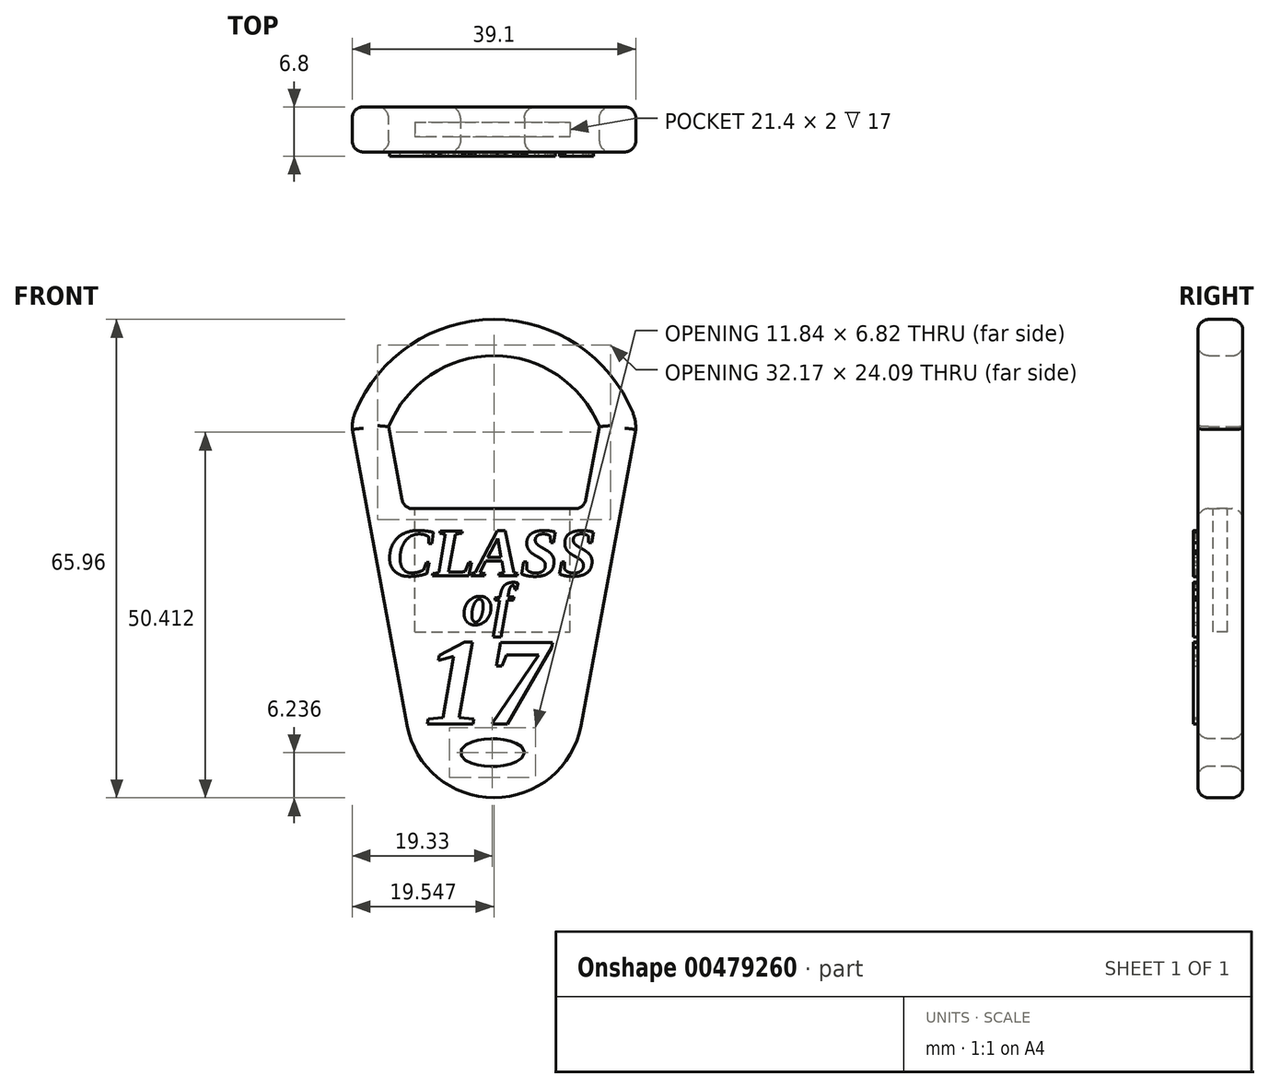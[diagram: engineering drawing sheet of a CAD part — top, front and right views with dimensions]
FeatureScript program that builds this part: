
annotation { "Feature Type Name" : "Feature", "Feature Type Description" : "" }
export const myFeature = defineFeature(function(context is Context, id is Id, definition is map)
    precondition{}
    {
        {
            var Q0;
            Q0=qCreatedBy(makeId("Front.planeOp"),FACE);
            var sketch = newSketch(context, id + "F0", { "sketchPlane" : qUnion([Q0])});
            skLineSegment(sketch, "E0", {"start": v(0.22, 53.5) * mm, "end": v(0.22, -27.22) * mm, "construction": true});
            skLineSegment(sketch, "E1", {"start": v(19.76, 12.33) * mm, "end": v(12.22, -28.48) * mm});
            skLineSegment(sketch, "E2.MirrorCS", {"start": v(-19.33, 12.33) * mm, "end": v(-11.78, -28.48) * mm});
            skLineSegment(sketch, "E3.0", {"start": v(-14.31, 12.71) * mm, "end": v(-12.22, 1.4) * mm});
            skLineSegment(sketch, "E3.3", {"start": v(14.75, 12.71) * mm, "end": v(12.66, 1.4) * mm});
            skLineSegment(sketch, "E4", {"start": v(-12.22, 1.4) * mm, "end": v(12.66, 1.4) * mm});
            skPoint(sketch, "E5", {"position": v(0.22, 20.6) * mm});
            skPoint(sketch, "E6", {"position": v(-14.31, 12.71) * mm});
            skPoint(sketch, "E7.MirrorP", {"position": v(14.75, 12.71) * mm});
            skArc(sketch, "E8", {"start": v(14.75, 12.71) * mm, "mid": v(0.22, 22.5) * mm, "end": v(-14.31, 12.71) * mm});
            skArc(sketch, "E9.0", {"start": v(19.62, 13.97) * mm, "mid": v(0.56, 27.5) * mm, "end": v(-18.94, 14.6) * mm});
            skArc(sketch, "E10", {"start": v(-18.94, 14.6) * mm, "mid": v(-19.26, 13.5) * mm, "end": v(-19.33, 12.33) * mm});
            skArc(sketch, "E11.MirrorCS", {"start": v(19.38, 14.6) * mm, "mid": v(19.7, 13.5) * mm, "end": v(19.76, 12.33) * mm});
            skPoint(sketch, "E12.orphan", {"position": v(-21.9, 26.19) * mm});
            skPoint(sketch, "E13.orphan", {"position": v(22.32, 26.19) * mm});
            skPoint(sketch, "E14.MirrorCS.start.orphan", {"position": v(0.22, 25.6) * mm});
            skArc(sketch, "E15", {"start": v(-11.78, -28.48) * mm, "mid": v(0.22, -38.46) * mm, "end": v(12.22, -28.48) * mm});
            skPoint(sketch, "E16.MirrorCS.end.orphan", {"position": v(0.22, -28.48) * mm});
            skPoint(sketch, "E16.MirrorCS.start.orphan", {"position": v(-11.78, -28.48) * mm});
            skLineSegment(sketch, "E17", {"start": v(-11.78, -28.48) * mm, "end": v(12.22, -28.48) * mm, "construction": true});
            skSolve(sketch);
        }
        {
            var Q0;
            Q0=qSketchRegion(id+"F0",true);
            extrude(context, id + "F1", {"entities" : qUnion([Q0]), "depth" : 6.2 * mm});
        }
        {
            var Q0;
            Q0=makeQuery(id+"F1.opExtrude","CAP_FACE",FACE,{"disambiguationData":[OSD([sQuery(id+"F0.wireOp",EDGE,"E1"),sQuery(id+"F0.wireOp",EDGE,"E2.MirrorCS"),sQuery(id+"F0.wireOp",EDGE,"E3.0"),sQuery(id+"F0.wireOp",EDGE,"E3.3"),sQuery(id+"F0.wireOp",EDGE,"E4"),sQuery(id+"F0.wireOp",EDGE,"E8"),sQuery(id+"F0.wireOp",EDGE,"E9.0"),sQuery(id+"F0.wireOp",EDGE,"E10"),sQuery(id+"F0.wireOp",EDGE,"E11.MirrorCS"),sQuery(id+"F0.wireOp",EDGE,"E15")])],"isStart":false});
            var sketch = newSketch(context, id + "F2", { "sketchPlane" : qUnion([Q0])});
            skEllipse(sketch, "E18", {"center": v(0, -32.22) * mm, "majorRadius": 4.42 * mm, "minorRadius": 1.9 * mm, "majorAxis": v(1, 0)});
            skSolve(sketch);
        }
        {
            var Q0;
            Q0=makeQuery(id+"F2.imprint","IMPRINT",FACE,{"disambiguationData":[TD([[makeQuery(id+"F2.imprint","IMPRINT",EDGE,{"derivedFrom":sQuery(id+"F2.wireOp",EDGE,"E18")}),1.0]])]});
            extrude(context, id + "F3", {"entities" : qUnion([Q0]), "operationType" : NewBodyOperationType.REMOVE, "oppositeDirection" : true, "depth" : 6.5 * mm});
        }
        {
            var Q0;
            Q0=makeQuery(id+"F1.opExtrude","SWEPT_FACE",FACE,{"disambiguationData":[OSD([sQuery(id+"F0.wireOp",EDGE,"E4")])]});
            var sketch = newSketch(context, id + "F4", { "sketchPlane" : qUnion([Q0])});
            skLineSegment(sketch, "E19", {"start": v(0, -2.1) * mm, "end": v(10.7, -2.1) * mm});
            skLineSegment(sketch, "E20.0", {"start": v(0, -4.1) * mm, "end": v(10.7, -4.1) * mm});
            skLineSegment(sketch, "E21", {"start": v(10.7, -2.1) * mm, "end": v(10.7, -4.1) * mm});
            skLineSegment(sketch, "E22", {"start": v(0, -2.1) * mm, "end": v(0, -4.1) * mm, "construction": true});
            skLineSegment(sketch, "E23.MirrorCS", {"start": v(0, -2.1) * mm, "end": v(-10.7, -2.1) * mm});
            skLineSegment(sketch, "E24.MirrorCS", {"start": v(-10.7, -2.1) * mm, "end": v(-10.7, -4.1) * mm});
            skLineSegment(sketch, "E25.MirrorCS", {"start": v(0, -4.1) * mm, "end": v(-10.7, -4.1) * mm});
            skSolve(sketch);
        }
        {
            var Q0;
            Q0=makeQuery(id+"F4.imprint","IMPRINT",FACE,{"disambiguationData":[TD([[makeQuery(id+"F4.imprint","IMPRINT",EDGE,{"derivedFrom":sQuery(id+"F4.wireOp",EDGE,"E19")}),-1.0]])]});
            extrude(context, id + "F5", {"entities" : qUnion([Q0]), "operationType" : NewBodyOperationType.REMOVE, "oppositeDirection" : true, "depth" : 17 * mm});
        }
        {
            var Q0;
            Q0=makeQuery(id+"F1.opExtrude","SWEPT_EDGE",EDGE,{"disambiguationData":[OSD([sQuery(id+"F0.wireOp",EDGE,"E3.0"),sQuery(id+"F0.wireOp",EDGE,"E4")])]});
            var Q1;
            Q1=makeQuery(id+"F1.opExtrude","SWEPT_EDGE",EDGE,{"disambiguationData":[OSD([sQuery(id+"F0.wireOp",EDGE,"E3.3"),sQuery(id+"F0.wireOp",EDGE,"E4")])]});
            var Q2;
            Q2=makeQuery(id+"F1.opExtrude","CAP_FACE",FACE,{"disambiguationData":[OSD([sQuery(id+"F0.wireOp",EDGE,"E1"),sQuery(id+"F0.wireOp",EDGE,"E2.MirrorCS"),sQuery(id+"F0.wireOp",EDGE,"E3.0"),sQuery(id+"F0.wireOp",EDGE,"E3.3"),sQuery(id+"F0.wireOp",EDGE,"E4"),sQuery(id+"F0.wireOp",EDGE,"E8"),sQuery(id+"F0.wireOp",EDGE,"E9.0"),sQuery(id+"F0.wireOp",EDGE,"E10"),sQuery(id+"F0.wireOp",EDGE,"E11.MirrorCS"),sQuery(id+"F0.wireOp",EDGE,"E15")])],"isStart":false});
            var Q3;
            Q3=makeQuery(id+"F1.opExtrude","CAP_FACE",FACE,{"disambiguationData":[OSD([sQuery(id+"F0.wireOp",EDGE,"E1"),sQuery(id+"F0.wireOp",EDGE,"E2.MirrorCS"),sQuery(id+"F0.wireOp",EDGE,"E3.0"),sQuery(id+"F0.wireOp",EDGE,"E3.3"),sQuery(id+"F0.wireOp",EDGE,"E4"),sQuery(id+"F0.wireOp",EDGE,"E8"),sQuery(id+"F0.wireOp",EDGE,"E9.0"),sQuery(id+"F0.wireOp",EDGE,"E10"),sQuery(id+"F0.wireOp",EDGE,"E11.MirrorCS"),sQuery(id+"F0.wireOp",EDGE,"E15")])],"isStart":true});
            fillet(context, id + "F6", {"entities" : qUnion([Q0, Q1, Q2, Q3]), "radius" : 1.5 * mm, "tangentPropagation" : true, "allowEdgeOverflow" : false});
        }
        {
            var Q0;
            Q0=makeQuery(id+"F1.opExtrude","CAP_FACE",FACE,{"disambiguationData":[OSD([sQuery(id+"F0.wireOp",EDGE,"E1"),sQuery(id+"F0.wireOp",EDGE,"E2.MirrorCS"),sQuery(id+"F0.wireOp",EDGE,"E3.0"),sQuery(id+"F0.wireOp",EDGE,"E3.3"),sQuery(id+"F0.wireOp",EDGE,"E4"),sQuery(id+"F0.wireOp",EDGE,"E8"),sQuery(id+"F0.wireOp",EDGE,"E9.0"),sQuery(id+"F0.wireOp",EDGE,"E10"),sQuery(id+"F0.wireOp",EDGE,"E11.MirrorCS"),sQuery(id+"F0.wireOp",EDGE,"E15")])],"isStart":false});
            var sketch = newSketch(context, id + "F7", { "sketchPlane" : qUnion([Q0])});
            skText(sketch, "E26", { "text": "CLASS", "fontName": "Tinos-BoldItalic.ttf"});
            skText(sketch, "E27", { "text": "of", "fontName": "Tinos-BoldItalic.ttf"});
            skText(sketch, "E28", { "text": "17", "fontName": "Tinos-BoldItalic.ttf"});
            const initialGuessF7  = {"E26": [-0.0145, -0.00785, 1, 0, 0.00679], "E27": [-0.00404, -0.01456, 1, 0, 0.00594], "E28": [-0.0094, -0.0283, 1, 0, 0.01234]};
            skSetInitialGuess(sketch, initialGuessF7);
            skSolve(sketch);
        }
        {
            var Q0;
            Q0=qSketchRegion(id+"F7",true);
            extrude(context, id + "F8", {"entities" : qUnion([Q0]), "operationType" : NewBodyOperationType.ADD, "depth" : .6 * mm, "offsetDistance" : 25 * mm});
        }
    });
